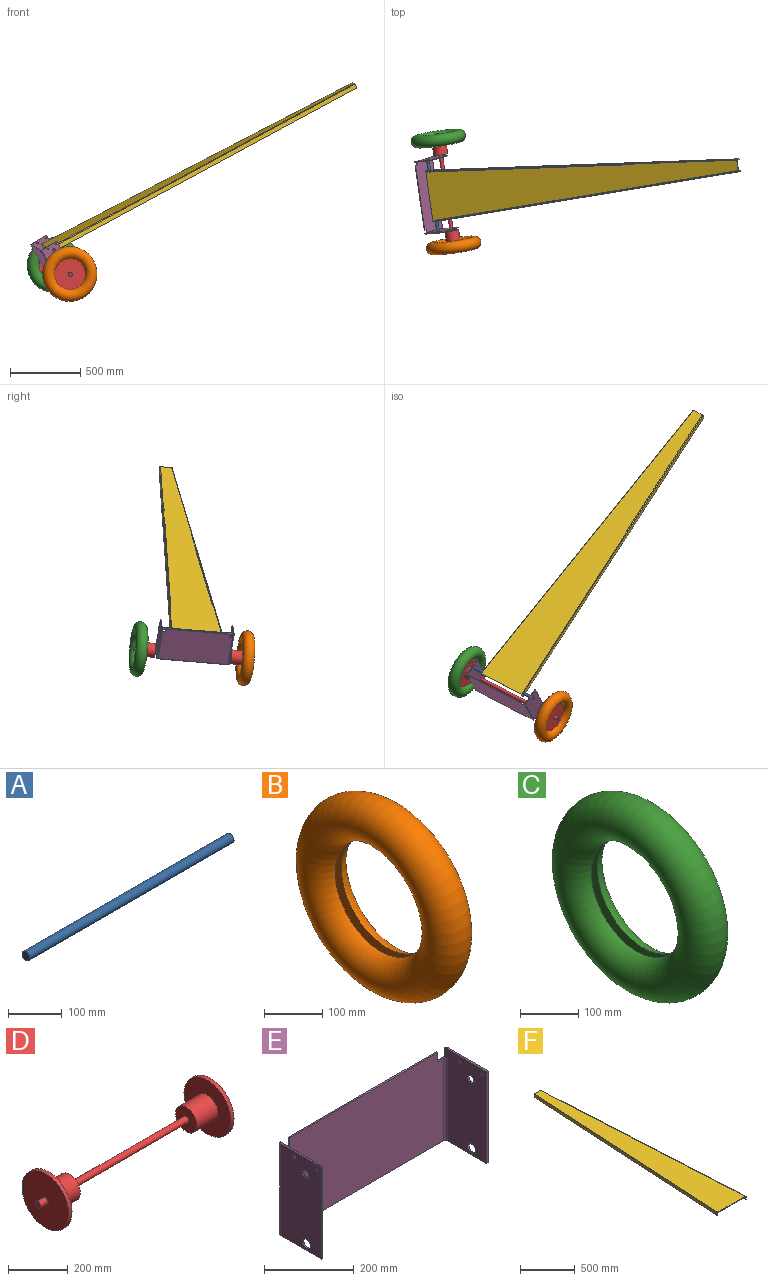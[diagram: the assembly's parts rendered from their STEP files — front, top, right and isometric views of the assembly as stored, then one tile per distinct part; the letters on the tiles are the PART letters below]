
ASSEMBLY  parts=6 mates=5
PART A: 3 faces, bbox 540x20x20 mm
  f0: cylinder r=10mm len=540mm, axis (-1,0,0), area 33929.2mm2, adj f1,f2
  f1: plane 20x20mm, normal (1,0,0), area 314.2mm2, adj f0
  f2: plane 20x20mm, normal (-1,0,0), area 314.2mm2, adj f0
PART B: 4 faces, bbox 85x422.1x422.1 mm
  f0: torus R=152.5mm, axis (-1,0,0), area 245426.6mm2, adj f1,f3
  f1: plane 305x305mm, normal (-1,0,0), area 34586mm2, adj f0,f2
  f2: cylinder r=152.5mm len=305mm, axis (-1,0,0), area 14372.8mm2, adj f1,f3
  f3: plane 305x305mm, normal (1,0,0), area 34586mm2, adj f0,f2
PART C: 4 faces, bbox 85x422.1x422.1 mm
  f0: torus R=152.5mm, axis (1,0,0), area 245426.6mm2, adj f1,f3
  f1: plane 305x305mm, normal (1,0,0), area 34586mm2, adj f0,f2
  f2: cylinder r=152.5mm len=305mm, axis (1,0,0), area 14372.8mm2, adj f1,f3
  f3: plane 305x305mm, normal (-1,0,0), area 34586mm2, adj f0,f2
PART D: 15 faces, bbox 850x264.8x264.8 mm
  f0: cylinder r=12.5mm len=550mm, axis (-1,0,0), area 43196.9mm2, adj f2,f9
  f1: cylinder r=50mm len=100mm, axis (-1,0,0), area 31415.9mm2, adj f2,f5
  f2: plane 100x100mm, normal (-1,0,0), area 7363.1mm2, adj f0,f1
  f3: plane 221.33x221.33mm, normal (1,0,0), area 37984.8mm2, adj f4,f7
  f4: torus R=152.5mm, axis (1,0,0), area 10442.9mm2, adj f3,f5
  f5: plane 221.33x221.33mm, normal (-1,0,0), area 30621.7mm2, adj f1,f4
  f6: plane 25x25mm, normal (1,0,0), area 490.9mm2, adj f7
  f7: cylinder r=12.5mm len=35mm, axis (-1,0,0), area 2748.9mm2, adj f3,f6
  f8: cylinder r=50mm len=100mm, axis (1,0,0), area 31415.9mm2, adj f9,f12
  f9: plane 100x100mm, normal (1,0,0), area 7363.1mm2, adj f0,f8
  f10: plane 221.33x221.33mm, normal (-1,0,0), area 37984.8mm2, adj f11,f14
  f11: torus R=152.5mm, axis (-1,0,0), area 10442.9mm2, adj f10,f12
  f12: plane 221.33x221.33mm, normal (1,0,0), area 30621.7mm2, adj f8,f11
  f13: plane 25x25mm, normal (-1,0,0), area 490.9mm2, adj f14
  f14: cylinder r=12.5mm len=35mm, axis (-1,0,0), area 2748.9mm2, adj f10,f13
PART E: 28 faces, bbox 523x134x250 mm
  f0: plane 505x250mm, normal (0,-1,0), area 125250mm2, adj f2,f11,f20,f21,f22,f23,f24,f25
  f1: plane 133.9x4mm, normal (0,0,1), area 530.7mm2, adj f4,f8,f9,f27
  f2: plane 465x4mm, normal (0,0,1), area 1860mm2, adj f0,f3,f20,f22
  f3: plane 513x250mm, normal (0,1,0), area 127050mm2, adj f2,f11,f20,f21,f22,f23,f26,f27
  f4: plane 250x133.9mm, normal (1,0,0), area 30566.9mm2, adj f1,f9,f11,f16,f17,f18,f19,f23
  f5: plane 250x133.9mm, normal (-1,0,0), area 30566.9mm2, adj f6,f10,f11,f12,f13,f14,f15,f21
  f6: plane 250x4mm, normal (0,-1,0), area 1000mm2, adj f5,f7,f10,f11
  f7: plane 250x129mm, normal (1,0,0), area 31344.4mm2, adj f6,f10,f11,f12,f13,f14,f15,f26
  f8: plane 250x129mm, normal (-1,0,0), area 31344.4mm2, adj f1,f9,f11,f16,f17,f18,f19,f27
  f9: plane 250x4mm, normal (0,-1,0), area 1000mm2, adj f1,f4,f8,f11
  f10: plane 133.9x4mm, normal (0,0,1), area 530.7mm2, adj f5,f6,f7,f26
  f11: plane 523x134mm, normal (0,0,-1), area 3132mm2, adj f0,f3,f4,f5,f6,f7,f8,f9
  f12: cylinder r=10mm len=20mm, axis (-1,0,0), area 251.3mm2, adj f5,f7
  f13: cylinder r=12.5mm len=25mm, axis (-1,0,0), area 314.2mm2, adj f5,f7
  f14: cylinder r=4mm len=8mm, axis (-1,0,0), area 100.5mm2, adj f5,f7
  f15: cylinder r=4mm len=8mm, axis (-1,0,0), area 100.5mm2, adj f5,f7
  f16: cylinder r=10mm len=20mm, axis (-1,0,0), area 251.3mm2, adj f4,f8
  f17: cylinder r=12.5mm len=25mm, axis (-1,0,0), area 314.2mm2, adj f4,f8
  f18: cylinder r=4mm len=8mm, axis (-1,0,0), area 100.5mm2, adj f4,f8
  f19: cylinder r=4mm len=8mm, axis (-1,0,0), area 100.5mm2, adj f4,f8
  f20: plane 25x4mm, normal (1,0,0), area 100mm2, adj f0,f2,f3,f21
  f21: plane 25x9mm, normal (0,0,1), area 105.3mm2, adj f0,f3,f5,f20,f25,f26
  f22: plane 25x4mm, normal (-1,0,0), area 100mm2, adj f0,f2,f3,f23
  f23: plane 25x9mm, normal (0,0,1), area 105.3mm2, adj f0,f3,f4,f22,f24,f27
  f24: cylinder r=5mm len=225mm, axis (0,0,1), area 1767.1mm2, adj f0,f4,f11,f23
  f25: cylinder r=5mm len=225mm, axis (0,0,1), area 1767.1mm2, adj f0,f5,f11,f21
  f26: cylinder r=5mm len=250mm, axis (0,0,-1), area 1938.3mm2, adj f3,f5,f7,f10,f11,f21
  f27: cylinder r=5mm len=250mm, axis (0,0,-1), area 1938.3mm2, adj f1,f3,f4,f8,f11,f23
PART F: 20 faces, bbox 370.9x2497.5x35.9 mm
  f0: plane 2496.08x140mm, normal (-1,0.06,0), area 74619.3mm2, adj f1,f3,f7,f11,f19
  f1: plane 370.12x35.12mm, normal (0,-1,0), area 2150.5mm2, adj f0,f2,f4,f5,f6,f7,f8,f9
  f2: plane 2496.08x140mm, normal (1,0.06,0), area 74619.3mm2, adj f1,f3,f9,f10,f18
  f3: plane 90.12x35.12mm, normal (0,1,0), area 750.5mm2, adj f0,f2,f4,f5,f6,f7,f8,f9
  f4: plane 2496.08x359.98mm, normal (0,0,1), area 549097.7mm2, adj f1,f3,f18,f19
  f5: plane 2496.08x350.64mm, normal (0,0,-1), area 524120mm2, adj f1,f3,f12,f13,f14,f15,f16,f17
  f6: plane 2496.94x140.87mm, normal (1,-0.06,0), area 62158.3mm2, adj f1,f3,f7,f11,f12,f14
  f7: plane 2496.08x145.01mm, normal (0,0,-1), area 12500mm2, adj f0,f1,f3,f6
  f8: plane 2496.94x140.87mm, normal (-1,-0.06,0), area 62158.3mm2, adj f1,f3,f9,f10,f15,f17
  f9: plane 2496.08x145.01mm, normal (0,0,-1), area 12500mm2, adj f1,f2,f3,f8
  f10: cylinder r=11mm len=22mm, axis (1,0,0), area 338.2mm2, adj f2,f8,f16
  f11: cylinder r=11mm len=22mm, axis (1,0,0), area 354.1mm2, adj f0,f6,f13
  f12: cylinder r=5mm len=2468.59mm, axis (0.06,1,0), area 19415.4mm2, adj f3,f5,f6,f13
  f13: bspline ~19.07x6.73mm, area 86.4mm2, adj f5,f11,f12,f14
  f14: cylinder r=5mm len=12.23mm, axis (0.06,1,0), area 92.9mm2, adj f1,f5,f6,f13
  f15: cylinder r=5mm len=12.23mm, axis (0.06,-1,0), area 92.9mm2, adj f1,f5,f8,f16
  f16: bspline ~19.07x6.67mm, area 86.4mm2, adj f5,f10,f15,f17
  f17: cylinder r=5mm len=2468.59mm, axis (0.06,-1,0), area 19415.4mm2, adj f3,f5,f8,f16
  f18: cylinder r=5mm len=2496.64mm, axis (0.06,-1,0), area 19635mm2, adj f1,f2,f3,f4
  f19: cylinder r=5mm len=2496.64mm, axis (0.06,1,0), area 19635mm2, adj f0,f1,f3,f4
PLACE A rot(axis=(0.33,-0.2,-0.92),87.7deg) t=(2878.13,-602.97,2346.17)mm
PLACE B rot(axis=(-0.64,-0.76,0.11),162.7deg) t=(-315.88,-884.34,234.07)mm
PLACE C rot(axis=(-0.64,-0.76,0.11),162.7deg) t=(-316.95,-876.94,234.7)mm
PLACE D rot(axis=(-0.64,-0.76,0.11),162.7deg) t=(-315.88,-884.34,234.07)mm
PLACE E rot(axis=(-0.18,-0.29,0.94),100.5deg) t=(-378.02,-887.46,177.52)mm
PLACE F rot(axis=(0.3,-0.18,-0.93),86.9deg) t=(2961.89,-576.51,2192.91)mm fixed
MATE revolute A.f0 <-> F.f10  axis (-0.14,0.99,0.08) through (-410.56,-910.02,393.88)mm
MATE fastened B.f0 <-> D.f1  axis (0.14,-0.99,-0.08) through (-261.63,-1261.61,202.01)mm
MATE fastened D.f1 <-> C.f0  axis (-0.14,0.99,0.08) through (-371.2,-499.67,266.76)mm
MATE revolute E.f13 <-> D.f0  axis (-0.14,0.99,0.08) through (-353.12,-625.43,256.07)mm
MATE fastened E.f12 <-> A.f0  axis (0.14,-0.99,-0.08) through (-373.68,-1166.46,372.09)mm
